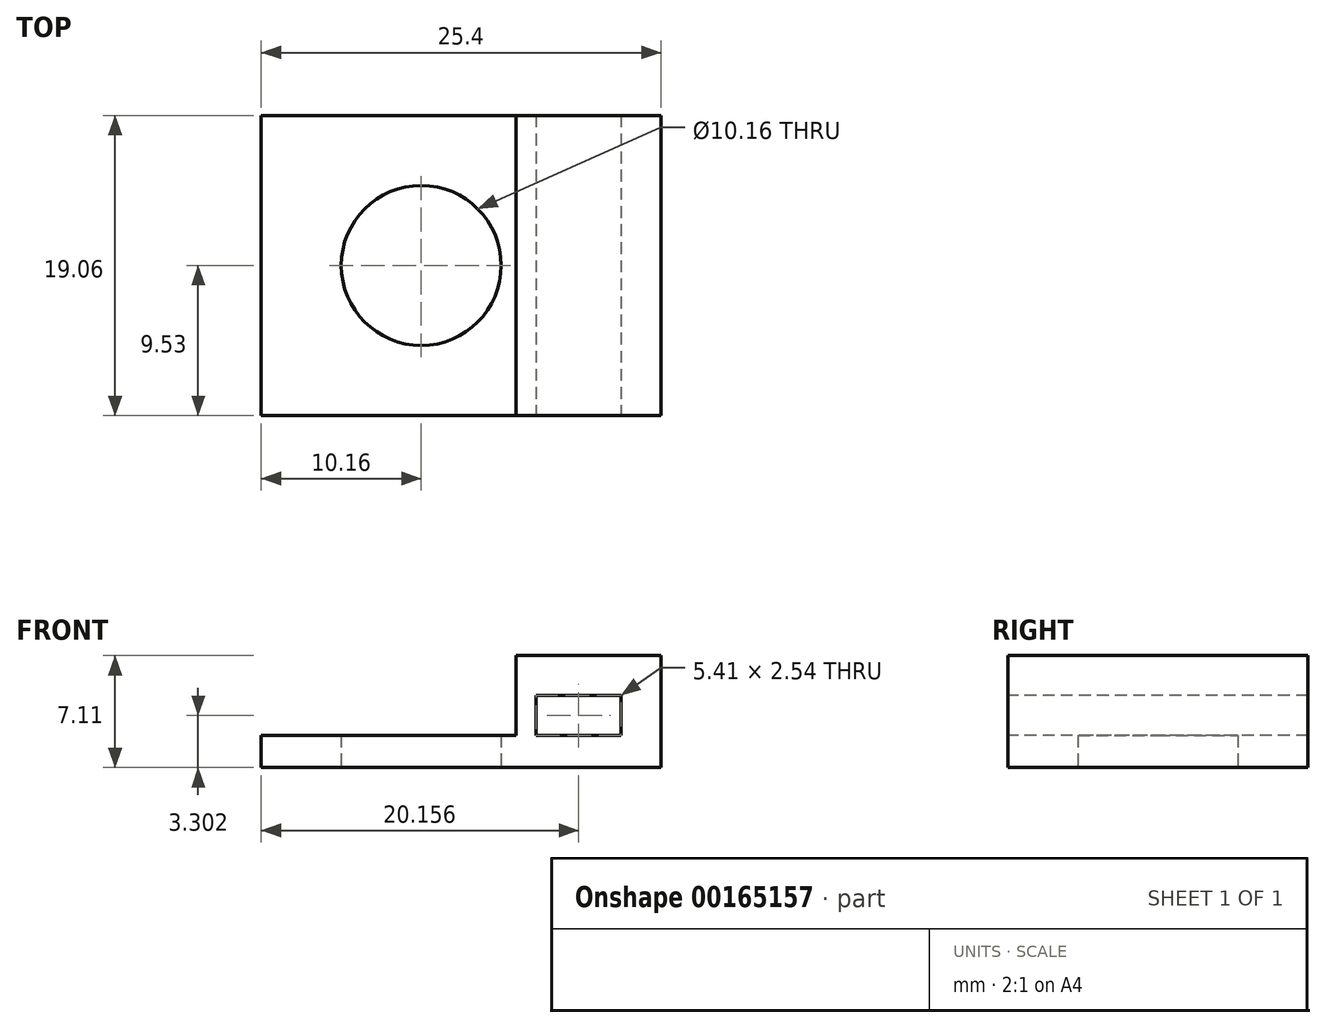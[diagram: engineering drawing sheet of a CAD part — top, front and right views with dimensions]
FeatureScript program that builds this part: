
annotation { "Feature Type Name" : "Feature", "Feature Type Description" : "" }
export const myFeature = defineFeature(function(context is Context, id is Id, definition is map)
    precondition{}
    {
        {
            var Q0;
            Q0=qCreatedBy(makeId("Top.planeOp"),FACE);
            var sketch = newSketch(context, id + "F0", { "sketchPlane" : qUnion([Q0])});
            skLineSegment(sketch, "E0.bottom", {"start": v(12.7, -9.52) * mm, "end": v(-12.7, -9.53) * mm});
            skLineSegment(sketch, "E0.top", {"start": v(12.7, 9.53) * mm, "end": v(-12.7, 9.53) * mm});
            skLineSegment(sketch, "E0.left", {"start": v(12.7, -9.52) * mm, "end": v(12.7, 9.53) * mm});
            skLineSegment(sketch, "E0.right", {"start": v(-12.7, -9.53) * mm, "end": v(-12.7, 9.53) * mm});
            skPoint(sketch, "E0.middle", {"position": v(0, 0) * mm});
            skCircle(sketch, "E1", {"center": v(-2.54, 0) * mm, "radius": 5.08 * mm});
            skSolve(sketch);
        }
        {
            var Q0;
            Q0 = qSketchRegion(id + "F0", true);
            extrude(context, id + "F1", {"entities" : qUnion([Q0]), "depth" : 2.03 * mm});
        }
        {
            var Q0;
            Q0=makeQuery(id+"F1.opExtrude","SWEPT_FACE",FACE,{"disambiguationData":[OSD([sQuery(id+"F0.wireOp",EDGE,"E0.bottom")])]});
            var sketch = newSketch(context, id + "F2", { "sketchPlane" : qUnion([Q0])});
            skLineSegment(sketch, "E2", {"start": v(12.7, 2.03) * mm, "end": v(12.7, 7.11) * mm});
            skLineSegment(sketch, "E3", {"start": v(12.7, 7.11) * mm, "end": v(3.48, 7.11) * mm});
            skLineSegment(sketch, "E4", {"start": v(3.48, 7.11) * mm, "end": v(3.48, 2.03) * mm});
            skLineSegment(sketch, "E5", {"start": v(3.48, 2.03) * mm, "end": v(4.75, 2.03) * mm});
            skLineSegment(sketch, "E6", {"start": v(4.75, 2.03) * mm, "end": v(4.75, 4.57) * mm});
            skLineSegment(sketch, "E7", {"start": v(4.75, 4.57) * mm, "end": v(10.16, 4.57) * mm});
            skLineSegment(sketch, "E8", {"start": v(10.16, 4.57) * mm, "end": v(10.16, 2.03) * mm});
            skLineSegment(sketch, "E9", {"start": v(10.16, 2.03) * mm, "end": v(12.7, 2.03) * mm});
            skSolve(sketch);
        }
        {
            var Q0;
            Q0 = qSketchRegion(id + "F2", true);
            var Q1;
            Q1=makeQuery(id+"F1.opExtrude","SWEPT_FACE",FACE,{"disambiguationData":[OSD([sQuery(id+"F0.wireOp",EDGE,"E0.top")])]});
            extrude(context, id + "F3", {"entities" : qUnion([Q0]), "operationType" : NewBodyOperationType.ADD, "endBound" : BoundingType.UP_TO_SURFACE, "oppositeDirection" : true, "endBoundEntityFace" : qUnion([Q1]), "depth" : 25.4 * mm});
        }
    });
